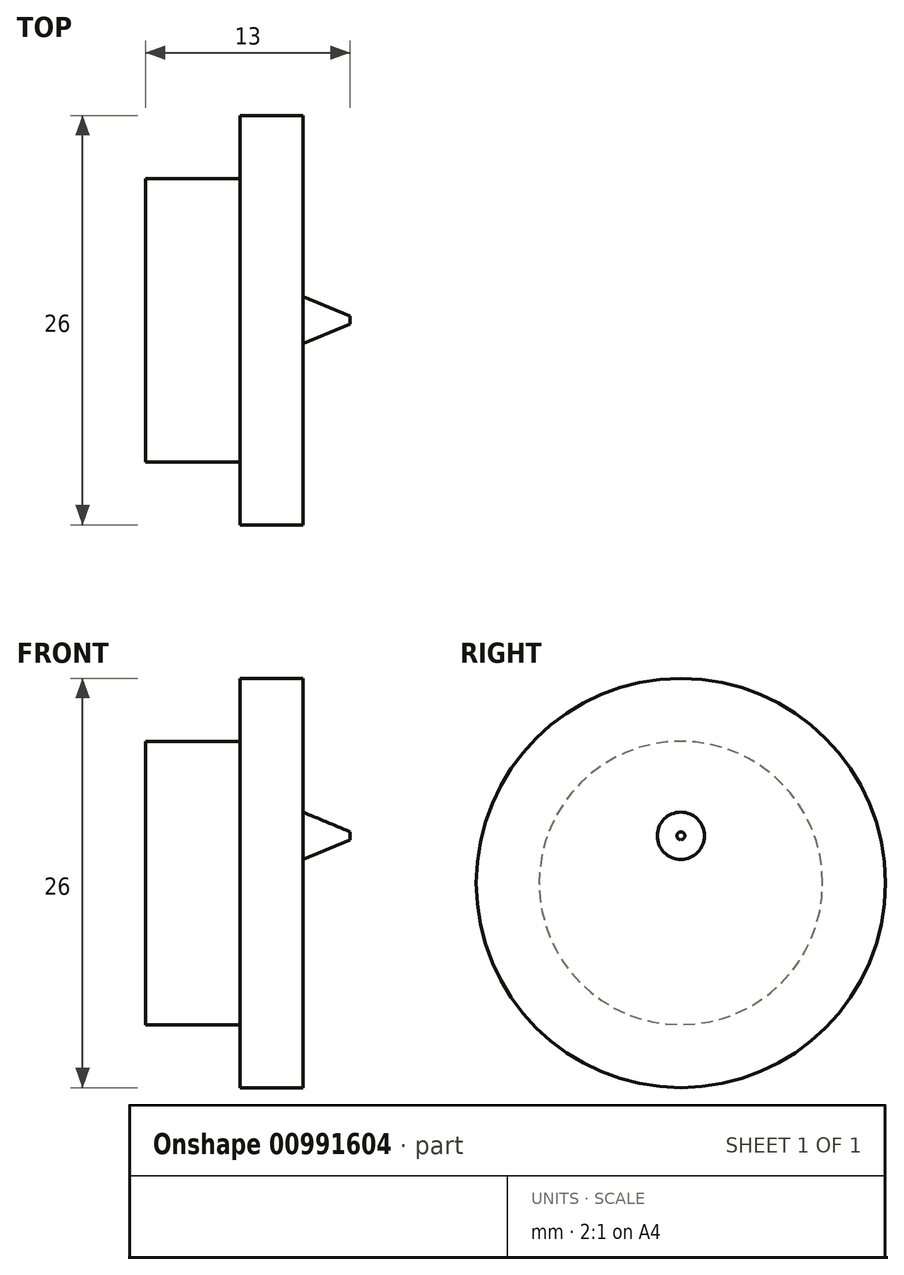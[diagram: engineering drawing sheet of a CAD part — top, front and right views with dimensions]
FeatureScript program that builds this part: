
annotation { "Feature Type Name" : "Feature", "Feature Type Description" : "" }
export const myFeature = defineFeature(function(context is Context, id is Id, definition is map)
    precondition{}
    {
        {
            var Q0;
            Q0=qCreatedBy(makeId("Top.planeOp"),FACE);
            var sketch = newSketch(context, id + "F0", { "sketchPlane" : qUnion([Q0])});
            skLineSegment(sketch, "E0", {"start": v(0, 0) * mm, "end": v(10, 0) * mm});
            skLineSegment(sketch, "E1", {"start": v(10, 0) * mm, "end": v(10, 13) * mm});
            skLineSegment(sketch, "E2", {"start": v(0, 0) * mm, "end": v(0, 9) * mm});
            skLineSegment(sketch, "E3", {"start": v(0, 9) * mm, "end": v(6, 9) * mm});
            skLineSegment(sketch, "E4", {"start": v(-1.6, 0) * mm, "end": v(16.6, 0) * mm, "construction": true});
            skLineSegment(sketch, "E5", {"start": v(6, 9) * mm, "end": v(6, 13) * mm});
            skLineSegment(sketch, "E6", {"start": v(6, 13) * mm, "end": v(10, 13) * mm});
            skSolve(sketch);
        }
        {
            var Q0;
            Q0=makeQuery(id+"F0.imprint","IMPRINT",FACE,{"disambiguationData":[TD([[makeQuery(id+"F0.imprint","IMPRINT",EDGE,{"derivedFrom":sQuery(id+"F0.wireOp",EDGE,"E0")}),1.0]])]});
            var Q1;
            Q1=sQuery(id+"F0.wireOp",EDGE,"E0");
            revolve(context, id + "F1", {"surfaceOperationType" : NewSurfaceOperationType.NEW, "entities" : qUnion([Q0]), "axis" : qUnion([Q1]), "revolveType" : RevolveType.FULL});
        }
        {
            var Q0;
            Q0=qCreatedBy(makeId("Front.planeOp"),FACE);
            var sketch = newSketch(context, id + "F2", { "sketchPlane" : qUnion([Q0])});
            skLineSegment(sketch, "E7", {"start": v(10, 3) * mm, "end": v(13, 3) * mm});
            skLineSegment(sketch, "E8", {"start": v(13, 3) * mm, "end": v(13, 3.25) * mm});
            skLineSegment(sketch, "E9", {"start": v(13, 3.25) * mm, "end": v(10, 4.5) * mm});
            skLineSegment(sketch, "E10", {"start": v(10, 4.5) * mm, "end": v(10, 3) * mm});
            skSolve(sketch);
        }
        {
            var Q0;
            Q0=makeQuery(id+"F2.imprint","IMPRINT",FACE,{"disambiguationData":[TD([[makeQuery(id+"F2.imprint","IMPRINT",EDGE,{"derivedFrom":sQuery(id+"F2.wireOp",EDGE,"E7")}),1.0]])]});
            var Q1;
            Q1=sQuery(id+"F2.wireOp",EDGE,"E7");
            revolve(context, id + "F3", {"operationType" : NewBodyOperationType.ADD, "surfaceOperationType" : NewSurfaceOperationType.NEW, "entities" : qUnion([Q0]), "axis" : qUnion([Q1]), "revolveType" : RevolveType.FULL});
        }
    });
